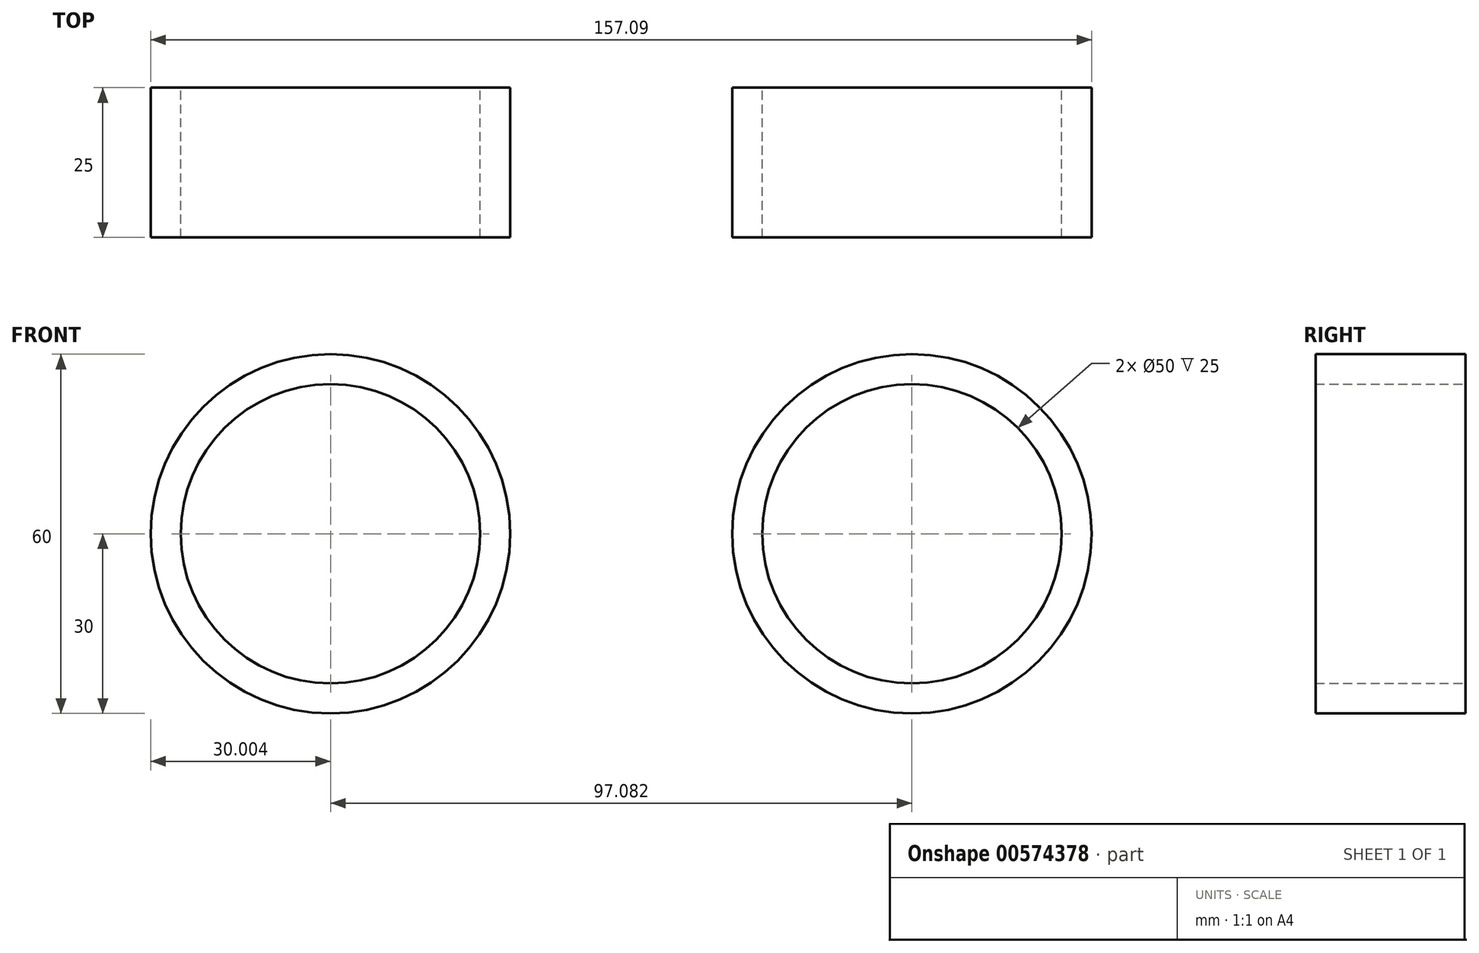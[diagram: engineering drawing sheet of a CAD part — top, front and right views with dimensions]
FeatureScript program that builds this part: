
annotation { "Feature Type Name" : "Feature", "Feature Type Description" : "" }
export const myFeature = defineFeature(function(context is Context, id is Id, definition is map)
    precondition{}
    {
        {
            var Q0;
            Q0=qCreatedBy(makeId("Front.planeOp"),FACE);
            var sketch = newSketch(context, id + "F0", { "sketchPlane" : qUnion([Q0])});
            skCircle(sketch, "E0", {"center": v(-48.4, 0) * mm, "radius": 30 * mm});
            skCircle(sketch, "E1", {"center": v(-48.4, 0) * mm, "radius": 25 * mm});
            skCircle(sketch, "E2", {"center": v(48.69, 0) * mm, "radius": 30 * mm});
            skCircle(sketch, "E3", {"center": v(48.69, 0) * mm, "radius": 25 * mm});
            skSolve(sketch);
        }
        {
            var Q0;
            Q0=makeQuery(id+"F0.imprint","IMPRINT",FACE,{"disambiguationData":[TD([[makeQuery(id+"F0.imprint","IMPRINT",EDGE,{"derivedFrom":sQuery(id+"F0.wireOp",EDGE,"E0")}),1.0]])]});
            var Q1;
            Q1=makeQuery(id+"F0.imprint","IMPRINT",FACE,{"disambiguationData":[TD([[makeQuery(id+"F0.imprint","IMPRINT",EDGE,{"derivedFrom":sQuery(id+"F0.wireOp",EDGE,"E2")}),1.0]])]});
            extrude(context, id + "F1", {"entities" : qUnion([Q0, Q1]), "depth" : 25 * mm, "offsetDistance" : 25 * mm});
        }
    });
